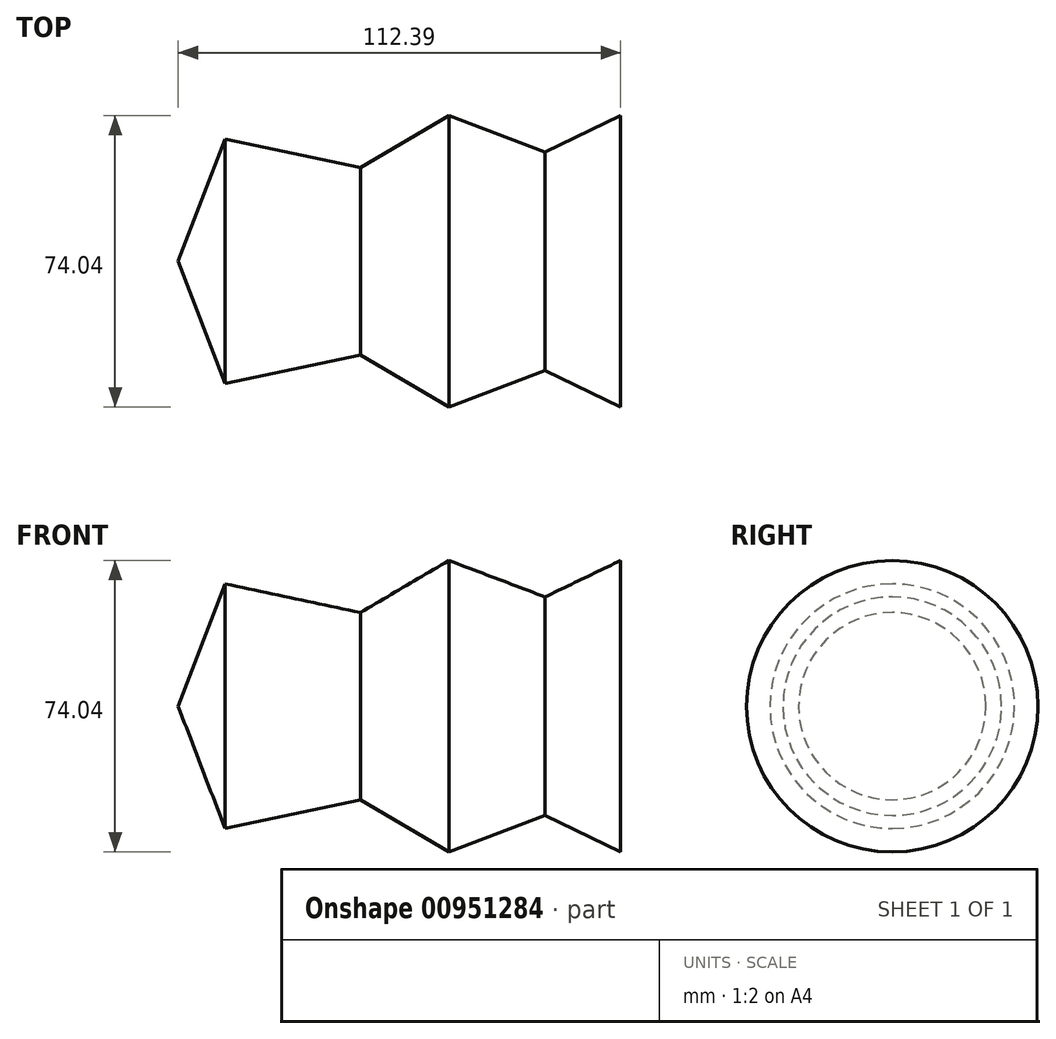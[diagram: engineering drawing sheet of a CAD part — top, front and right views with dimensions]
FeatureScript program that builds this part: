
annotation { "Feature Type Name" : "Feature", "Feature Type Description" : "" }
export const myFeature = defineFeature(function(context is Context, id is Id, definition is map)
    precondition{}
    {
        {
            var Q0;
            Q0=qCreatedBy(makeId("Front.planeOp"),FACE);
            var sketch = newSketch(context, id + "F0", { "sketchPlane" : qUnion([Q0])});
            skLineSegment(sketch, "E0", {"start": v(36.83, 51.9) * mm, "end": v(149.22, 51.9) * mm});
            skLineSegment(sketch, "E1", {"start": v(149.22, 51.9) * mm, "end": v(149.22, 14.89) * mm});
            skLineSegment(sketch, "E2", {"start": v(149.22, 14.89) * mm, "end": v(130.04, 24.14) * mm});
            skLineSegment(sketch, "E3", {"start": v(130.04, 24.14) * mm, "end": v(105.58, 14.89) * mm});
            skLineSegment(sketch, "E4", {"start": v(105.58, 14.89) * mm, "end": v(83.1, 28.1) * mm});
            skLineSegment(sketch, "E5", {"start": v(83.1, 28.1) * mm, "end": v(48.73, 20.84) * mm});
            skLineSegment(sketch, "E6", {"start": v(48.73, 20.84) * mm, "end": v(36.83, 51.9) * mm});
            skSolve(sketch);
        }
        {
            var Q0;
            Q0 = qSketchRegion(id + "F0", true);
            var Q1;
            Q1=sQuery(id+"F0.wireOp",EDGE,"E0");
            revolve(context, id + "F1", {"surfaceOperationType" : NewSurfaceOperationType.NEW, "entities" : qUnion([Q0]), "axis" : qUnion([Q1]), "revolveType" : RevolveType.FULL});
        }
    });
